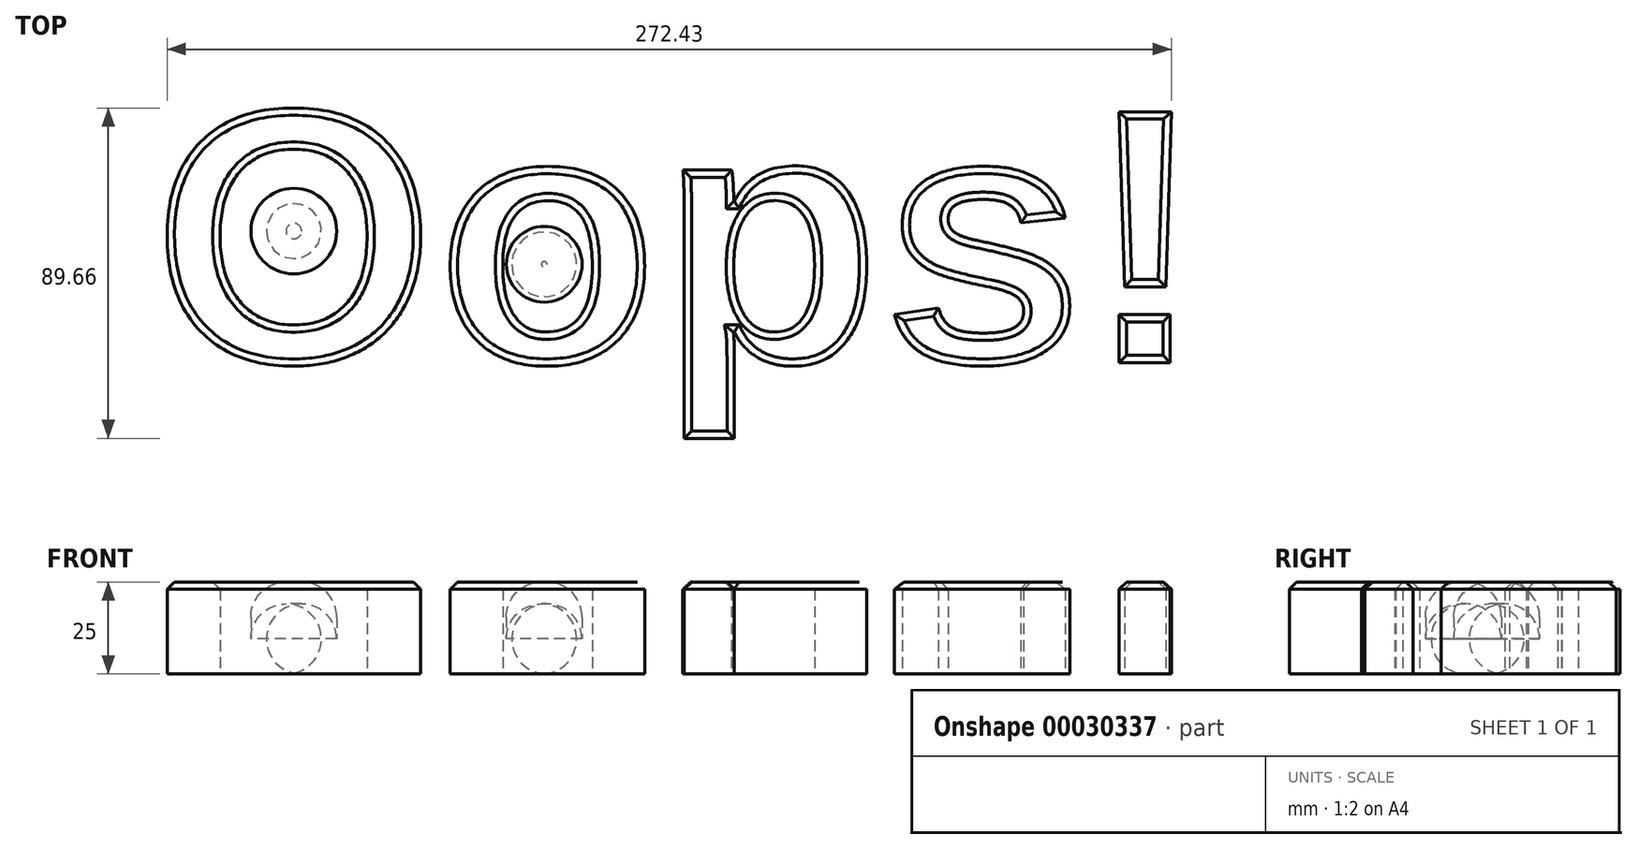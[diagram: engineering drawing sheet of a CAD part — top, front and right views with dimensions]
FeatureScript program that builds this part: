
annotation { "Feature Type Name" : "Feature", "Feature Type Description" : "" }
export const myFeature = defineFeature(function(context is Context, id is Id, definition is map)
    precondition{}
    {
        {
            var Q0;
            Q0=qCreatedBy(makeId("Top.planeOp"),FACE);
            var sketch = newSketch(context, id + "F0", { "sketchPlane" : qUnion([Q0])});
            skText(sketch, "E0", { "text": "Oops!", "fontName": "Arimo-Bold.ttf"});
            skCircle(sketch, "E1", {"center": v(-43.97, -11.59) * mm, "radius": 11.63 * mm});
            skCircle(sketch, "E2", {"center": v(23.95, -20.6) * mm, "radius": 10.27 * mm});
            const initialGuessF0  = {"E0": [-0.0824, -0.04729, 1, 0, 0.07127]};
            skSetInitialGuess(sketch, initialGuessF0);
            skSolve(sketch);
        }
        {
            var Q0;
            Q0 = qSketchRegion(id + "F0", true);
            var Q1;
            Q1=makeQuery(id+"F0.imprint","IMPRINT",FACE,{"disambiguationData":[TD([[makeQuery(id+"F0.imprint","IMPRINT",EDGE,{"derivedFrom":sQuery(id+"F0.wireOp",EDGE,"E1")}),1.0]])]});
            var Q2;
            Q2=makeQuery(id+"F0.imprint","IMPRINT",FACE,{"disambiguationData":[TD([[makeQuery(id+"F0.imprint","IMPRINT",EDGE,{"derivedFrom":sQuery(id+"F0.wireOp",EDGE,"E2")}),1.0]])]});
            extrude(context, id + "F1", {"entities" : qUnion([Q0, Q1, Q2]), "depth" : 25 * mm});
        }
        {
            var Q0;
            Q0=makeQuery(id+"F1.opExtrude","CAP_EDGE",EDGE,{"disambiguationData":[OSD([sQuery(id+"F0.wireOp",EDGE,"E1")])],"isStart":false});
            var Q1;
            Q1=makeQuery(id+"F1.opExtrude","CAP_EDGE",EDGE,{"disambiguationData":[OSD([sQuery(id+"F0.wireOp",EDGE,"E2")])],"isStart":false});
            var Q2;
            Q2=makeQuery(id+"F1.opExtrude","CAP_EDGE",EDGE,{"disambiguationData":[OSD([sQuery(id+"F0.wireOp",EDGE,"E2")])],"isStart":true});
            var Q3;
            Q3=makeQuery(id+"F1.opExtrude","CAP_EDGE",EDGE,{"disambiguationData":[OSD([sQuery(id+"F0.wireOp",EDGE,"E1")])],"isStart":true});
            fillet(context, id + "F2", {"entities" : qUnion([Q0, Q1, Q2, Q3]), "radius" : 9.53 * mm, "tangentPropagation" : true, "allowEdgeOverflow" : false});
        }
        {
            var Q0;
            Q0=makeQuery(id+"F1.opExtrude","CAP_FACE",FACE,{"disambiguationData":[OSD([sQuery(id+"F0.wireOp",EDGE,"E0.sketch_text.stroke-0"),sQuery(id+"F0.wireOp",EDGE,"E0.sketch_text.stroke-1"),sQuery(id+"F0.wireOp",EDGE,"E0.sketch_text.stroke-2"),sQuery(id+"F0.wireOp",EDGE,"E0.sketch_text.stroke-3"),sQuery(id+"F0.wireOp",EDGE,"E0.sketch_text.stroke-4"),sQuery(id+"F0.wireOp",EDGE,"E0.sketch_text.stroke-5"),sQuery(id+"F0.wireOp",EDGE,"E0.sketch_text.stroke-6"),sQuery(id+"F0.wireOp",EDGE,"E0.sketch_text.stroke-7"),sQuery(id+"F0.wireOp",EDGE,"E0.sketch_text.stroke-8"),sQuery(id+"F0.wireOp",EDGE,"E0.sketch_text.stroke-9"),sQuery(id+"F0.wireOp",EDGE,"E0.sketch_text.stroke-10"),sQuery(id+"F0.wireOp",EDGE,"E0.sketch_text.stroke-11"),sQuery(id+"F0.wireOp",EDGE,"E0.sketch_text.stroke-12"),sQuery(id+"F0.wireOp",EDGE,"E0.sketch_text.stroke-13"),sQuery(id+"F0.wireOp",EDGE,"E0.sketch_text.stroke-14"),sQuery(id+"F0.wireOp",EDGE,"E0.sketch_text.stroke-15"),sQuery(id+"F0.wireOp",EDGE,"E0.sketch_text.stroke-16")])],"isStart":false});
            var Q1;
            Q1=makeQuery(id+"F1.opExtrude","CAP_FACE",FACE,{"disambiguationData":[OSD([sQuery(id+"F0.wireOp",EDGE,"E0.sketch_text.stroke-17"),sQuery(id+"F0.wireOp",EDGE,"E0.sketch_text.stroke-18"),sQuery(id+"F0.wireOp",EDGE,"E0.sketch_text.stroke-19"),sQuery(id+"F0.wireOp",EDGE,"E0.sketch_text.stroke-20"),sQuery(id+"F0.wireOp",EDGE,"E0.sketch_text.stroke-21"),sQuery(id+"F0.wireOp",EDGE,"E0.sketch_text.stroke-22"),sQuery(id+"F0.wireOp",EDGE,"E0.sketch_text.stroke-23"),sQuery(id+"F0.wireOp",EDGE,"E0.sketch_text.stroke-24"),sQuery(id+"F0.wireOp",EDGE,"E0.sketch_text.stroke-25"),sQuery(id+"F0.wireOp",EDGE,"E0.sketch_text.stroke-26"),sQuery(id+"F0.wireOp",EDGE,"E0.sketch_text.stroke-27"),sQuery(id+"F0.wireOp",EDGE,"E0.sketch_text.stroke-28"),sQuery(id+"F0.wireOp",EDGE,"E0.sketch_text.stroke-29"),sQuery(id+"F0.wireOp",EDGE,"E0.sketch_text.stroke-30")])],"isStart":false});
            var Q2;
            Q2=makeQuery(id+"F1.opExtrude","CAP_FACE",FACE,{"disambiguationData":[OSD([sQuery(id+"F0.wireOp",EDGE,"E0.sketch_text.stroke-31"),sQuery(id+"F0.wireOp",EDGE,"E0.sketch_text.stroke-32"),sQuery(id+"F0.wireOp",EDGE,"E0.sketch_text.stroke-33"),sQuery(id+"F0.wireOp",EDGE,"E0.sketch_text.stroke-34"),sQuery(id+"F0.wireOp",EDGE,"E0.sketch_text.stroke-35"),sQuery(id+"F0.wireOp",EDGE,"E0.sketch_text.stroke-36"),sQuery(id+"F0.wireOp",EDGE,"E0.sketch_text.stroke-37"),sQuery(id+"F0.wireOp",EDGE,"E0.sketch_text.stroke-38"),sQuery(id+"F0.wireOp",EDGE,"E0.sketch_text.stroke-39"),sQuery(id+"F0.wireOp",EDGE,"E0.sketch_text.stroke-40"),sQuery(id+"F0.wireOp",EDGE,"E0.sketch_text.stroke-41"),sQuery(id+"F0.wireOp",EDGE,"E0.sketch_text.stroke-42"),sQuery(id+"F0.wireOp",EDGE,"E0.sketch_text.stroke-43"),sQuery(id+"F0.wireOp",EDGE,"E0.sketch_text.stroke-44"),sQuery(id+"F0.wireOp",EDGE,"E0.sketch_text.stroke-45"),sQuery(id+"F0.wireOp",EDGE,"E0.sketch_text.stroke-46"),sQuery(id+"F0.wireOp",EDGE,"E0.sketch_text.stroke-47"),sQuery(id+"F0.wireOp",EDGE,"E0.sketch_text.stroke-48"),sQuery(id+"F0.wireOp",EDGE,"E0.sketch_text.stroke-49"),sQuery(id+"F0.wireOp",EDGE,"E0.sketch_text.stroke-50"),sQuery(id+"F0.wireOp",EDGE,"E0.sketch_text.stroke-51"),sQuery(id+"F0.wireOp",EDGE,"E0.sketch_text.stroke-52"),sQuery(id+"F0.wireOp",EDGE,"E0.sketch_text.stroke-53")])],"isStart":false});
            var Q3;
            Q3=makeQuery(id+"F1.opExtrude","CAP_FACE",FACE,{"disambiguationData":[OSD([sQuery(id+"F0.wireOp",EDGE,"E0.sketch_text.stroke-54"),sQuery(id+"F0.wireOp",EDGE,"E0.sketch_text.stroke-55"),sQuery(id+"F0.wireOp",EDGE,"E0.sketch_text.stroke-56"),sQuery(id+"F0.wireOp",EDGE,"E0.sketch_text.stroke-57"),sQuery(id+"F0.wireOp",EDGE,"E0.sketch_text.stroke-58"),sQuery(id+"F0.wireOp",EDGE,"E0.sketch_text.stroke-59"),sQuery(id+"F0.wireOp",EDGE,"E0.sketch_text.stroke-60"),sQuery(id+"F0.wireOp",EDGE,"E0.sketch_text.stroke-61"),sQuery(id+"F0.wireOp",EDGE,"E0.sketch_text.stroke-62"),sQuery(id+"F0.wireOp",EDGE,"E0.sketch_text.stroke-63"),sQuery(id+"F0.wireOp",EDGE,"E0.sketch_text.stroke-64"),sQuery(id+"F0.wireOp",EDGE,"E0.sketch_text.stroke-65"),sQuery(id+"F0.wireOp",EDGE,"E0.sketch_text.stroke-66"),sQuery(id+"F0.wireOp",EDGE,"E0.sketch_text.stroke-67"),sQuery(id+"F0.wireOp",EDGE,"E0.sketch_text.stroke-68"),sQuery(id+"F0.wireOp",EDGE,"E0.sketch_text.stroke-69"),sQuery(id+"F0.wireOp",EDGE,"E0.sketch_text.stroke-70"),sQuery(id+"F0.wireOp",EDGE,"E0.sketch_text.stroke-71"),sQuery(id+"F0.wireOp",EDGE,"E0.sketch_text.stroke-72"),sQuery(id+"F0.wireOp",EDGE,"E0.sketch_text.stroke-73"),sQuery(id+"F0.wireOp",EDGE,"E0.sketch_text.stroke-74"),sQuery(id+"F0.wireOp",EDGE,"E0.sketch_text.stroke-75"),sQuery(id+"F0.wireOp",EDGE,"E0.sketch_text.stroke-76"),sQuery(id+"F0.wireOp",EDGE,"E0.sketch_text.stroke-77"),sQuery(id+"F0.wireOp",EDGE,"E0.sketch_text.stroke-78"),sQuery(id+"F0.wireOp",EDGE,"E0.sketch_text.stroke-79"),sQuery(id+"F0.wireOp",EDGE,"E0.sketch_text.stroke-80"),sQuery(id+"F0.wireOp",EDGE,"E0.sketch_text.stroke-81"),sQuery(id+"F0.wireOp",EDGE,"E0.sketch_text.stroke-82")])],"isStart":false});
            var Q4;
            Q4=makeQuery(id+"F1.opExtrude","CAP_FACE",FACE,{"disambiguationData":[OSD([sQuery(id+"F0.wireOp",EDGE,"E0.sketch_text.stroke-83"),sQuery(id+"F0.wireOp",EDGE,"E0.sketch_text.stroke-84"),sQuery(id+"F0.wireOp",EDGE,"E0.sketch_text.stroke-85"),sQuery(id+"F0.wireOp",EDGE,"E0.sketch_text.stroke-86")])],"isStart":false});
            var Q5;
            Q5=makeQuery(id+"F1.opExtrude","CAP_FACE",FACE,{"disambiguationData":[OSD([sQuery(id+"F0.wireOp",EDGE,"E0.sketch_text.stroke-87"),sQuery(id+"F0.wireOp",EDGE,"E0.sketch_text.stroke-88"),sQuery(id+"F0.wireOp",EDGE,"E0.sketch_text.stroke-89"),sQuery(id+"F0.wireOp",EDGE,"E0.sketch_text.stroke-90")])],"isStart":false});
            chamfer(context, id + "F3", {"entities" : qUnion([Q0, Q1, Q2, Q3, Q4, Q5]), "width" : 2 * mm, "tangentPropagation" : true});
        }
    });
